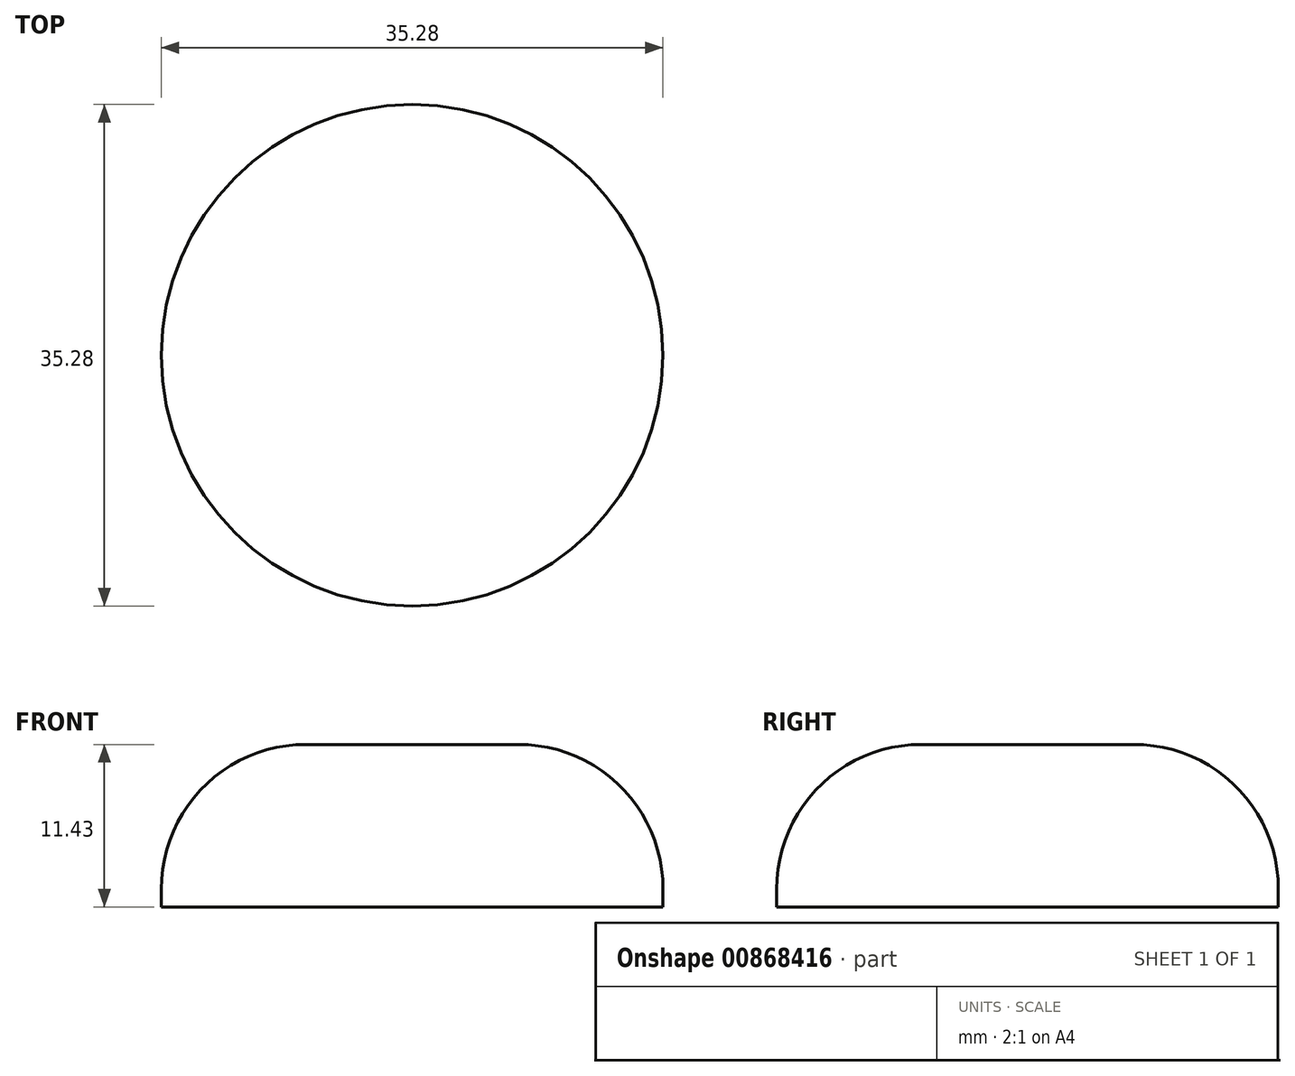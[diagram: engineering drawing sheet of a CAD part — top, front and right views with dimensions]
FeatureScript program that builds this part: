
annotation { "Feature Type Name" : "Feature", "Feature Type Description" : "" }
export const myFeature = defineFeature(function(context is Context, id is Id, definition is map)
    precondition{}
    {
        {
            var Q0;
            Q0=qCreatedBy(makeId("Top.planeOp"),FACE);
            var sketch = newSketch(context, id + "F0", { "sketchPlane" : qUnion([Q0])});
            skCircle(sketch, "E0", {"center": v(0, 0) * mm, "radius": 17.64 * mm});
            skSolve(sketch);
        }
        {
            var Q0;
            Q0=makeQuery(id+"F0.imprint","IMPRINT",FACE,{"disambiguationData":[TD([[makeQuery(id+"F0.imprint","IMPRINT",EDGE,{"derivedFrom":sQuery(id+"F0.wireOp",EDGE,"E0")}),1.0]])]});
            var Q1;
            Q1=sQuery(id+"F0.wireOp",EDGE,"E0");
            extrude(context, id + "F1", {"entities" : qUnion([Q0]), "surfaceEntities" : qUnion([Q1]), "depth" : 11.43 * mm, "offsetDistance" : 25.4 * mm});
        }
        {
            var Q0;
            Q0=makeQuery(id+"F1.opExtrude","CAP_FACE",FACE,{"disambiguationData":[OSD([sQuery(id+"F0.wireOp",EDGE,"E0")])],"isStart":false});
            fillet(context, id + "F2", {"entities" : qUnion([Q0]), "radius" : 10.16 * mm, "tangentPropagation" : true, "allowEdgeOverflow" : false});
        }
    });
